# Revit family: Herkules ER20_Fugenprofile mit Sinuswelle Sanierungsfugenprofil
name_source: partatom
category: Generic Models
units: mm (PartAtom-declared; Revit-internal decimal feet)

## family parameters
Always vertical = No
Can host rebar = No
Cut with Voids When Loaded = No
Part Type = Normal
Room Calculation Point = No
Round Connector Dimension = Use Diameter
Shared = No
Work Plane-Based = Yes

## types (3) — shared parameters
Adresse = Iglauer Str. 6 86316 Friedberg
Basismaterial Herkules = Stahl S355 JR
Description = Joint profiles reconstruction and transition
Höhe = 14 mm  [stored 0.0459318 ft]
Keynote = Herkules ER20
Lieferzeit = 2 weeks
Manufacturer = Guggemos GmbH
Model = Heavy duty profile for reconstruction of industrial concrete floor slabs
Telefon = +49 (0)8 21 / 455 969 0
Type Image = Herkules ER20_Foto.jpg (2)
URL = https://www.fugenprofile.de
Video = https://www.youtube.com
zero-valued in all types: Default Elevation

## per-type parameters (varying)
| type | Länge | Type Comments |
| ER20_L2500 | 2500 mm  [stored 8.2021 ft] | HerkulesER20_L2500 |
| ER20_L2000 | 2000 mm  [stored 6.56168 ft] | HerkulesER20_L2000 |
| ER20_L1500 | 1500 mm  [stored 4.92126 ft] | HerkulesER20_L2000 |

note: [stored X ft] marks values corroborated as IEEE doubles in the binary element streams (Revit-internal decimal feet)

## geometry (parser evidence)
native form markers: Sweep x11
no freeform markers — native parametric forms only
